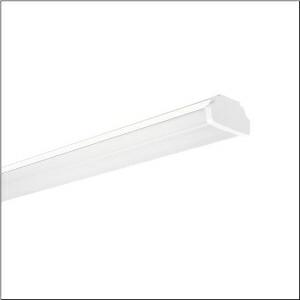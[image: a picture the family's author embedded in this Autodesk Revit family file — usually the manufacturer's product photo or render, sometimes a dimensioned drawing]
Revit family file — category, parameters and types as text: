
# Revit family: modario_r__31_ho_53bm812c1v6105_fe2c
name_source: partatom
category: Lighting Fixtures
units: mm (PartAtom-declared; Revit-internal decimal feet)

## family parameters
Cut with Voids When Loaded = No
Host = Face
Light Source = No
Part Type = Normal
Room Calculation Point = No
Round Connector Dimension = Use Diameter
Shared = No

## types (1)
- --- (1 x LED, 10560 lm, 63.8 W, 6500K)
    Apparent Load = 64 VA
    CIE Flux Codes = 47 80 95 92 100
    Color Rendering = 80
    Color Temperature = 6500K
    Default Elevation = 1800 mm
    Description = Modario® 31 HOluminaire insert, length: 1.495mm, width: 81mm, height: 82mm, LED rated luminous flux: 10.560lm, light colour: 865, control gear: ON/OFF Multilumen, CLOi, control gear: ECG Multilumen, with plug, 3-pole, with phase selection, mains connection: 220..240V, AC, 50/60Hz, primary optical cover: cover, of PMMA, light emission: direct distribution, primary light characteristic: symmetric, protection rating (complete): IP20, protection rating (LED compartment): IP50, insulation class (complete): insulation class I (protective earthing), certification: CE, ENEC, VDE, UKCA, permissible ambient temperature for indoor applications: -35..+35°C, corresponds to IFS (International Featured Standards) requirements for safety and quality in the food industry, reducing of maximum allowable ambient temperature of 5°C with ceiling mounting, packaging unit: 1 piece
    Height = 92 mm
    Lamp = 1 x LED
    Lamp Light Flux = 10560 lm
    Lamp Power = 63.8 W
    Lamp count = 1
    Length = 1495 mm
    Luminous efficacy = 166 lm/W
    Manufacturer = Siteco
    ModVariant = No
    Model = 53BM812C1V6105
    Mounting Place = Ceiling
    Mounting Type = Pendant
    Number of Poles = 1
    OnlyDefault = Yes
    Power Factor = 1
    Product Name = Modario® 31 HO
    Product group = luminaire insert
    ProductGroupID = 902
    Protection Class = Protection class I
    Protection Degree = IP 20
    RLX_Detail_Level = 1
    RlxData = <blob elided: 39809 chars, md5=a0c92709>
    Socket = socket
    Standby Power = 0 W
    System Light Flux = 10560 lm
    System Power = 64 W
    Type Comments = factory setting: luminous flux: 100 % | (A | C | E) | 144 mA
    Type Image = l_1003447.jpg
    URL = http://relux.com
    VarID = @adj_131285
    Voltage = 0 V
    Weight = 0.00 kg
    Width = 81 mm

## geometry (parser evidence)
native form markers: Blend x4, Sweep x12
no freeform markers — native parametric forms only
